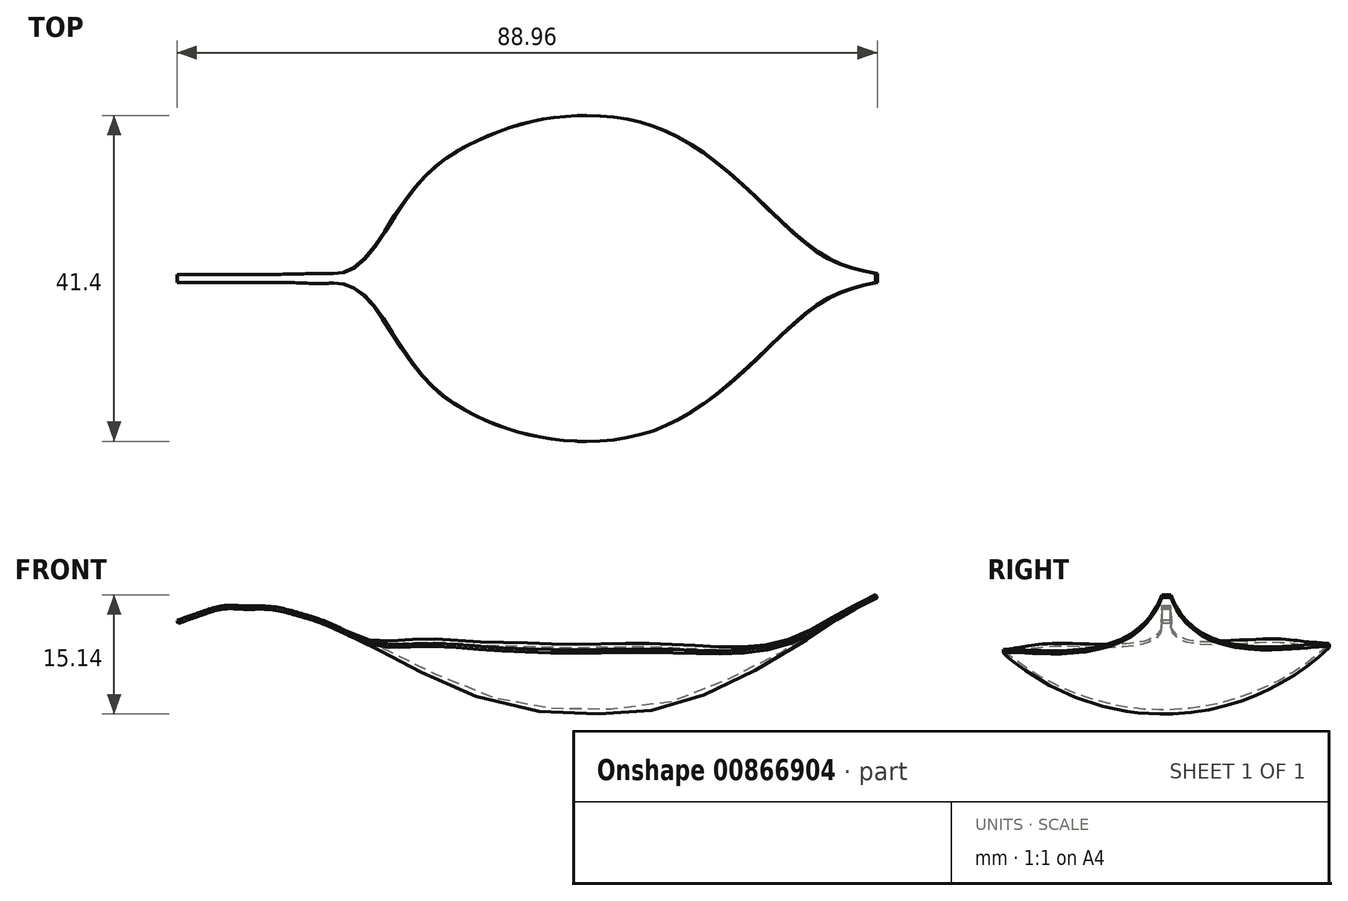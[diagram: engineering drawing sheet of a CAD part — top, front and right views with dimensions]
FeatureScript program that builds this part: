
annotation { "Feature Type Name" : "Feature", "Feature Type Description" : "" }
export const myFeature = defineFeature(function(context is Context, id is Id, definition is map)
    precondition{}
    {
        {
            var Q0;
            Q0=qCreatedBy(makeId("Front.planeOp"),FACE);
            var sketch = newSketch(context, id + "F0", { "sketchPlane" : qUnion([Q0])});
            skLineSegment(sketch, "E0", {"start": v(-44.39, 4.16) * mm, "end": v(-44.26, 3.85) * mm});
            skLineSegment(sketch, "E1", {"start": v(-44.39, 4.16) * mm, "end": v(-43.46, 4.53) * mm});
            skLineSegment(sketch, "E2", {"start": v(-41.78, 6.45) * mm, "end": v(-40.67, 3.2) * mm});
            skLineSegment(sketch, "E3", {"start": v(-38.43, 7.01) * mm, "end": v(-38.1, 3.57) * mm});
            skLineSegment(sketch, "E4", {"start": v(-35.95, 7.18) * mm, "end": v(-35.95, 3.55) * mm});
            skLineSegment(sketch, "E5", {"start": v(-32.27, 7.01) * mm, "end": v(-33.3, 3.24) * mm});
            skLineSegment(sketch, "E6", {"start": v(-28.95, 6.26) * mm, "end": v(-30.33, 2.84) * mm});
            skLineSegment(sketch, "E7", {"start": v(-25.44, 5.2) * mm, "end": v(-27.02, 1.8) * mm});
            skLineSegment(sketch, "E8", {"start": v(-22.43, 4.2) * mm, "end": v(-24.29, 0.87) * mm});
            skLineSegment(sketch, "E9", {"start": v(-19.09, 3.54) * mm, "end": v(-21.1, -0.4) * mm});
            skLineSegment(sketch, "E10", {"start": v(-15.92, 2.85) * mm, "end": v(-17.86, -1.91) * mm});
            skLineSegment(sketch, "E11", {"start": v(-11.9, 2.91) * mm, "end": v(-14.28, -3.81) * mm});
            skLineSegment(sketch, "E12", {"start": v(-6.26, 2.97) * mm, "end": v(-8.48, -6.69) * mm});
            skLineSegment(sketch, "E13", {"start": v(-0.4, 2.8) * mm, "end": v(-2.27, -8.54) * mm});
            skLineSegment(sketch, "E14", {"start": v(6.22, 2.3) * mm, "end": v(6.22, -9.83) * mm});
            skLineSegment(sketch, "E15", {"start": v(12.31, 2.74) * mm, "end": v(14.01, -9.61) * mm});
            skLineSegment(sketch, "E16", {"start": v(18.98, 3.06) * mm, "end": v(21.7, -7.59) * mm});
            skLineSegment(sketch, "E17", {"start": v(25.17, 3.1) * mm, "end": v(28.49, -5.53) * mm});
            skLineSegment(sketch, "E18", {"start": v(29.75, 3.12) * mm, "end": v(32.65, -3.36) * mm});
            skLineSegment(sketch, "E19", {"start": v(34.44, 4.54) * mm, "end": v(37.33, -0.72) * mm});
            skLineSegment(sketch, "E20", {"start": v(38.64, 6.73) * mm, "end": v(41.5, 2.56) * mm});
            skLineSegment(sketch, "E21", {"start": v(43, 9.56) * mm, "end": v(45.94, 5.03) * mm});
            skSolve(sketch);
        }
        {
            var Q0;
            Q0=makeQuery(id+"FtduOgnOkjfPjRU.importOp","IMPORT",FACE,{"importTag":1.0});
            cPoint(context, id + "F1", {"pointType" : PointType.MESH_POINT, "mesh" : qUnion([Q0]), "x" : -44.4 * mm, "y" : 0.48 * mm, "z" : 4.17 * mm});
        }
        {
            var Q0;
            Q0=makeQuery(id+"FtduOgnOkjfPjRU.importOp","IMPORT",EDGE,{"importTag":0.0});
            cPoint(context, id + "F2", {"pointType" : PointType.MESH_POINT, "mesh" : qUnion([Q0]), "x" : -44.4 * mm, "y" : -0.48 * mm, "z" : 4.15 * mm});
        }
        {
            var Q0;
            Q0=qCreatedBy(id+"F1",VERTEX);
            var Q1;
            Q1=qCreatedBy(id+"F2",VERTEX);
            var Q2;
            Q2=sQuery(id+"F0.wireOp",VERTEX,"E0.end");
            cPlane(context, id + "F3", {"entities" : qUnion([Q0, Q1, Q2]), "cplaneType" : CPlaneType.THREE_POINT, "offset" : 25.4 * mm, "width" : 152.4 * mm, "height" : 152.4 * mm});
        }
        {
            var Q0;
            Q0=qCreatedBy(id+"F3.planeOp",FACE);
            var sketch = newSketch(context, id + "F4", { "sketchPlane" : qUnion([Q0])});
            skLineSegment(sketch, "E22.bottom", {"start": v(-0.3, 20.4) * mm, "end": v(0.7, 20.4) * mm});
            skLineSegment(sketch, "E22.top", {"start": v(-0.3, 20) * mm, "end": v(0.7, 20) * mm});
            skLineSegment(sketch, "E22.left", {"start": v(-0.3, 20.4) * mm, "end": v(-0.3, 20) * mm});
            skLineSegment(sketch, "E22.right", {"start": v(0.7, 20.4) * mm, "end": v(0.7, 20) * mm});
            skLineSegment(sketch, "E23", {"start": v(0.2, 20.4) * mm, "end": v(0.2, 20) * mm, "construction": true});
            skSolve(sketch);
        }
        {
            var Q0;
            Q0=qCreatedBy(id+"F3.planeOp",FACE);
            var Q1;
            Q1=sQuery(id+"F0.wireOp",EDGE,"E2");
            cPlane(context, id + "F5", {"entities" : qUnion([Q0, Q1]), "cplaneType" : CPlaneType.LINE_ANGLE, "offset" : 25.4 * mm, "angle" : 0 * degree, "width" : 152.4 * mm, "height" : 152.4 * mm});
        }
        {
            var Q0;
            Q0=qCreatedBy(id+"F5.planeOp",FACE);
            var sketch = newSketch(context, id + "F6", { "sketchPlane" : qUnion([Q0])});
            skLineSegment(sketch, "E24.bottom", {"start": v(0.32, 18.53) * mm, "end": v(-0.7, 18.53) * mm});
            skLineSegment(sketch, "E24.top", {"start": v(0.32, 18.12) * mm, "end": v(-0.7, 18.12) * mm});
            skLineSegment(sketch, "E24.left", {"start": v(0.32, 18.53) * mm, "end": v(0.32, 18.12) * mm});
            skLineSegment(sketch, "E24.right", {"start": v(-0.7, 18.53) * mm, "end": v(-0.7, 18.12) * mm});
            skLineSegment(sketch, "E25", {"start": v(-0.19, 18.53) * mm, "end": v(-0.19, 18.12) * mm, "construction": true});
            skLineSegment(sketch, "E26", {"start": v(-0.7, 18.33) * mm, "end": v(-0.19, 18.33) * mm, "construction": true});
            skSolve(sketch);
        }
        {
            var Q0;
            Q0=qCreatedBy(id+"F5.planeOp",FACE);
            var Q1;
            Q1=sQuery(id+"F0.wireOp",EDGE,"E3");
            cPlane(context, id + "F7", {"entities" : qUnion([Q0, Q1]), "cplaneType" : CPlaneType.LINE_ANGLE, "offset" : 25.4 * mm, "angle" : 0 * degree, "width" : 152.4 * mm, "height" : 152.4 * mm});
        }
        {
            var Q0;
            Q0=qCreatedBy(id+"F7.planeOp",FACE);
            var sketch = newSketch(context, id + "F8", { "sketchPlane" : qUnion([Q0])});
            skLineSegment(sketch, "E27.bottom", {"start": v(-0.3, 9.7) * mm, "end": v(0.71, 9.7) * mm});
            skLineSegment(sketch, "E27.top", {"start": v(-0.3, 9.3) * mm, "end": v(0.71, 9.3) * mm});
            skLineSegment(sketch, "E27.left", {"start": v(-0.3, 9.7) * mm, "end": v(-0.3, 9.3) * mm});
            skLineSegment(sketch, "E27.right", {"start": v(0.71, 9.7) * mm, "end": v(0.71, 9.3) * mm});
            skSolve(sketch);
        }
        {
            var Q0;
            Q0=sQuery(id+"F0.wireOp",EDGE,"E4");
            var Q1;
            Q1=qCreatedBy(id+"F7.planeOp",FACE);
            cPlane(context, id + "F9", {"entities" : qUnion([Q0, Q1]), "cplaneType" : CPlaneType.LINE_ANGLE, "offset" : 25.4 * mm, "angle" : 0 * degree, "width" : 152.4 * mm, "height" : 152.4 * mm});
        }
        {
            var Q0;
            Q0=qCreatedBy(id+"F9.planeOp",FACE);
            var sketch = newSketch(context, id + "F10", { "sketchPlane" : qUnion([Q0])});
            skLineSegment(sketch, "E28.bottom", {"start": v(0.32, 6.18) * mm, "end": v(-0.7, 6.18) * mm});
            skLineSegment(sketch, "E28.top", {"start": v(0.32, 5.77) * mm, "end": v(-0.7, 5.77) * mm});
            skLineSegment(sketch, "E28.left", {"start": v(0.32, 6.18) * mm, "end": v(0.32, 5.77) * mm});
            skLineSegment(sketch, "E28.right", {"start": v(-0.7, 6.18) * mm, "end": v(-0.7, 5.77) * mm});
            skLineSegment(sketch, "E29", {"start": v(-0.19, 6.18) * mm, "end": v(-0.19, 5.77) * mm, "construction": true});
            skLineSegment(sketch, "E30", {"start": v(-0.7, 5.97) * mm, "end": v(-0.19, 5.97) * mm, "construction": true});
            skSolve(sketch);
        }
        {
            var Q0;
            Q0=qCreatedBy(id+"F9.planeOp",FACE);
            var Q1;
            Q1=sQuery(id+"F0.wireOp",EDGE,"E5");
            cPlane(context, id + "F11", {"entities" : qUnion([Q0, Q1]), "cplaneType" : CPlaneType.LINE_ANGLE, "offset" : 25.4 * mm, "angle" : 0 * degree, "width" : 152.4 * mm, "height" : 152.4 * mm});
        }
        {
            var Q0;
            Q0=qCreatedBy(id+"F11.planeOp",FACE);
            var sketch = newSketch(context, id + "F12", { "sketchPlane" : qUnion([Q0])});
            skLineSegment(sketch, "E31.bottom", {"start": v(-0.34, -2.64) * mm, "end": v(0.7, -2.64) * mm});
            skLineSegment(sketch, "E31.top", {"start": v(-0.34, -3.05) * mm, "end": v(0.7, -3.05) * mm});
            skLineSegment(sketch, "E31.left", {"start": v(-0.34, -2.64) * mm, "end": v(-0.34, -3.05) * mm});
            skLineSegment(sketch, "E31.right", {"start": v(0.7, -2.64) * mm, "end": v(0.7, -3.05) * mm});
            skSolve(sketch);
        }
        {
            var Q0;
            Q0=qCreatedBy(id+"F11.planeOp",FACE);
            var Q1;
            Q1=sQuery(id+"F0.wireOp",EDGE,"E6");
            cPlane(context, id + "F13", {"entities" : qUnion([Q0, Q1]), "cplaneType" : CPlaneType.LINE_ANGLE, "offset" : 25.4 * mm, "angle" : 0 * degree, "width" : 152.4 * mm, "height" : 152.4 * mm});
        }
        {
            var Q0;
            Q0=qCreatedBy(id+"F13.planeOp",FACE);
            var sketch = newSketch(context, id + "F14", { "sketchPlane" : qUnion([Q0])});
            skLineSegment(sketch, "E32.bottom", {"start": v(0.4, -5.99) * mm, "end": v(-0.72, -5.99) * mm});
            skLineSegment(sketch, "E32.top", {"start": v(0.4, -6.4) * mm, "end": v(-0.72, -6.4) * mm});
            skLineSegment(sketch, "E32.left", {"start": v(0.4, -5.99) * mm, "end": v(0.4, -6.4) * mm});
            skLineSegment(sketch, "E32.right", {"start": v(-0.72, -5.99) * mm, "end": v(-0.72, -6.4) * mm});
            skSolve(sketch);
        }
        {
            var Q0;
            Q0=qCreatedBy(id+"F13.planeOp",FACE);
            var Q1;
            Q1=sQuery(id+"F0.wireOp",EDGE,"E7");
            cPlane(context, id + "F15", {"entities" : qUnion([Q0, Q1]), "cplaneType" : CPlaneType.LINE_ANGLE, "offset" : 25.4 * mm, "angle" : 0 * degree, "width" : 152.4 * mm, "height" : 152.4 * mm});
        }
        {
            var Q0;
            Q0=qCreatedBy(id+"F15.planeOp",FACE);
            var sketch = newSketch(context, id + "F16", { "sketchPlane" : qUnion([Q0])});
            skLineSegment(sketch, "E33.bottom", {"start": v(-0.5, -6.99) * mm, "end": v(0.77, -6.99) * mm});
            skLineSegment(sketch, "E33.top", {"start": v(-0.5, -7.4) * mm, "end": v(0.77, -7.4) * mm});
            skLineSegment(sketch, "E33.left", {"start": v(-0.5, -6.99) * mm, "end": v(-0.5, -7.4) * mm});
            skLineSegment(sketch, "E33.right", {"start": v(0.77, -6.99) * mm, "end": v(0.77, -7.4) * mm});
            skSolve(sketch);
        }
        {
            var Q0;
            Q0=qCreatedBy(id+"F15.planeOp",FACE);
            var Q1;
            Q1=sQuery(id+"F0.wireOp",EDGE,"E8");
            cPlane(context, id + "F17", {"entities" : qUnion([Q0, Q1]), "cplaneType" : CPlaneType.LINE_ANGLE, "offset" : 25.4 * mm, "angle" : 0 * degree, "width" : 152.4 * mm, "height" : 152.4 * mm});
        }
        {
            var Q0;
            Q0=qCreatedBy(id+"F17.planeOp",FACE);
            var sketch = newSketch(context, id + "F18", { "sketchPlane" : qUnion([Q0])});
            skLineSegment(sketch, "E34.bottom", {"start": v(0.68, -8.57) * mm, "end": v(-0.89, -8.57) * mm});
            skLineSegment(sketch, "E34.top", {"start": v(0.68, -8.97) * mm, "end": v(-0.89, -8.97) * mm});
            skLineSegment(sketch, "E34.left", {"start": v(0.68, -8.57) * mm, "end": v(0.68, -8.97) * mm});
            skLineSegment(sketch, "E34.right", {"start": v(-0.89, -8.57) * mm, "end": v(-0.89, -8.97) * mm});
            skSolve(sketch);
        }
        {
            var Q0;
            Q0=qCreatedBy(id+"F17.planeOp",FACE);
            var Q1;
            Q1=sQuery(id+"F0.wireOp",EDGE,"E9");
            cPlane(context, id + "F19", {"entities" : qUnion([Q0, Q1]), "cplaneType" : CPlaneType.LINE_ANGLE, "offset" : 25.4 * mm, "angle" : 0 * degree, "width" : 152.4 * mm, "height" : 152.4 * mm});
        }
        {
            var Q0;
            Q0=qCreatedBy(id+"F19.planeOp",FACE);
            var sketch = newSketch(context, id + "F20", { "sketchPlane" : qUnion([Q0])});
            skLineSegment(sketch, "E35", {"start": v(2.82, -7.57) * mm, "end": v(2.82, -7.97) * mm});
            skLineSegment(sketch, "E36", {"start": v(-3.04, -7.45) * mm, "end": v(-3.04, -7.86) * mm});
            skArc(sketch, "E37", {"start": v(-3.04, -7.86) * mm, "mid": v(-0.11, -8.09) * mm, "end": v(2.82, -7.97) * mm});
            skArc(sketch, "E38", {"start": v(-3.04, -7.45) * mm, "mid": v(-0.11, -7.68) * mm, "end": v(2.82, -7.57) * mm});
            skSolve(sketch);
        }
        {
            var Q0;
            Q0=qCreatedBy(id+"F19.planeOp",FACE);
            var Q1;
            Q1=sQuery(id+"F0.wireOp",EDGE,"E10");
            cPlane(context, id + "F21", {"entities" : qUnion([Q0, Q1]), "cplaneType" : CPlaneType.LINE_ANGLE, "offset" : 25.4 * mm, "angle" : 0 * degree, "width" : 152.4 * mm, "height" : 152.4 * mm});
        }
        {
            var Q0;
            Q0=qCreatedBy(id+"F21.planeOp",FACE);
            var sketch = newSketch(context, id + "F22", { "sketchPlane" : qUnion([Q0])});
            skLineSegment(sketch, "E39", {"start": v(8.5, -4.5) * mm, "end": v(8.5, -4.9) * mm});
            skLineSegment(sketch, "E40", {"start": v(-7.76, -5.08) * mm, "end": v(-7.76, -5.49) * mm});
            skArc(sketch, "E41", {"start": v(-7.76, -5.49) * mm, "mid": v(0.42, -6.68) * mm, "end": v(8.5, -4.9) * mm});
            skArc(sketch, "E42", {"start": v(-7.76, -5.08) * mm, "mid": v(0.42, -6.24) * mm, "end": v(8.5, -4.5) * mm});
            skSolve(sketch);
        }
        {
            var Q0;
            Q0=qCreatedBy(id+"F21.planeOp",FACE);
            var Q1;
            Q1=sQuery(id+"F0.wireOp",EDGE,"E11");
            cPlane(context, id + "F23", {"entities" : qUnion([Q0, Q1]), "cplaneType" : CPlaneType.LINE_ANGLE, "offset" : 25.4 * mm, "angle" : 0 * degree, "width" : 152.4 * mm, "height" : 152.4 * mm});
        }
        {
            var Q0;
            Q0=qCreatedBy(id+"F23.planeOp",FACE);
            var sketch = newSketch(context, id + "F24", { "sketchPlane" : qUnion([Q0])});
            skLineSegment(sketch, "E43", {"start": v(-13.64, -2.2) * mm, "end": v(-13.64, -2.6) * mm});
            skLineSegment(sketch, "E44", {"start": v(13.22, -2.84) * mm, "end": v(13.22, -3.24) * mm});
            skArc(sketch, "E45", {"start": v(-13.64, -2.6) * mm, "mid": v(-0.3, -6.56) * mm, "end": v(13.22, -3.24) * mm});
            skArc(sketch, "E46", {"start": v(-13.64, -2.2) * mm, "mid": v(-0.3, -6.03) * mm, "end": v(13.22, -2.84) * mm});
            skSolve(sketch);
        }
        {
            var Q0;
            Q0=qCreatedBy(id+"F23.planeOp",FACE);
            var Q1;
            Q1=sQuery(id+"F0.wireOp",EDGE,"E12");
            cPlane(context, id + "F25", {"entities" : qUnion([Q0, Q1]), "cplaneType" : CPlaneType.LINE_ANGLE, "offset" : 25.4 * mm, "angle" : 0 * degree, "width" : 152.4 * mm, "height" : 152.4 * mm});
        }
        {
            var Q0;
            Q0=qCreatedBy(id+"F25.planeOp",FACE);
            var sketch = newSketch(context, id + "F26", { "sketchPlane" : qUnion([Q0])});
            skLineSegment(sketch, "E47", {"start": v(17.36, 0.18) * mm, "end": v(17.36, -0.23) * mm});
            skLineSegment(sketch, "E48", {"start": v(-17.33, -0.44) * mm, "end": v(-17.33, -0.84) * mm});
            skArc(sketch, "E49", {"start": v(-17.33, -0.84) * mm, "mid": v(0.12, -6.34) * mm, "end": v(17.36, -0.23) * mm});
            skArc(sketch, "E50", {"start": v(-17.33, -0.44) * mm, "mid": v(0.12, -5.69) * mm, "end": v(17.36, 0.18) * mm});
            skSolve(sketch);
        }
        {
            var Q0;
            Q0=qCreatedBy(id+"F25.planeOp",FACE);
            var Q1;
            Q1=sQuery(id+"F0.wireOp",EDGE,"E13");
            cPlane(context, id + "F27", {"entities" : qUnion([Q0, Q1]), "cplaneType" : CPlaneType.LINE_ANGLE, "offset" : 25.4 * mm, "angle" : 0 * degree, "width" : 152.4 * mm, "height" : 152.4 * mm});
        }
        {
            var Q0;
            Q0=qCreatedBy(id+"F27.planeOp",FACE);
            var sketch = newSketch(context, id + "F28", { "sketchPlane" : qUnion([Q0])});
            skLineSegment(sketch, "E51", {"start": v(-19.65, 1.37) * mm, "end": v(-19.65, 0.96) * mm});
            skLineSegment(sketch, "E52", {"start": v(19.58, 0.61) * mm, "end": v(19.58, 0.2) * mm});
            skArc(sketch, "E53", {"start": v(-19.65, 0.96) * mm, "mid": v(-0.18, -6.9) * mm, "end": v(19.58, 0.2) * mm});
            skArc(sketch, "E54", {"start": v(-19.65, 1.37) * mm, "mid": v(-0.18, -6.32) * mm, "end": v(19.58, 0.61) * mm});
            skSolve(sketch);
        }
        {
            var Q0;
            Q0=sQuery(id+"F0.wireOp",EDGE,"E14");
            var Q1;
            Q1=qCreatedBy(id+"F27.planeOp",FACE);
            cPlane(context, id + "F29", {"entities" : qUnion([Q0, Q1]), "cplaneType" : CPlaneType.LINE_ANGLE, "offset" : 25.4 * mm, "angle" : 0 * degree, "width" : 152.4 * mm, "height" : 152.4 * mm});
        }
        {
            var Q0;
            Q0=qCreatedBy(id+"F29.planeOp",FACE);
            var sketch = newSketch(context, id + "F30", { "sketchPlane" : qUnion([Q0])});
            skLineSegment(sketch, "E55", {"start": v(20.7, 1.32) * mm, "end": v(20.7, 0.91) * mm});
            skLineSegment(sketch, "E56", {"start": v(-20.64, 0.61) * mm, "end": v(-20.64, 0.2) * mm});
            skArc(sketch, "E57", {"start": v(-20.64, 0.2) * mm, "mid": v(0.17, -7.5) * mm, "end": v(20.7, 0.91) * mm});
            skArc(sketch, "E58", {"start": v(-20.64, 0.61) * mm, "mid": v(0.17, -6.93) * mm, "end": v(20.7, 1.32) * mm});
            skSolve(sketch);
        }
        {
            var Q0;
            Q0=qCreatedBy(id+"F29.planeOp",FACE);
            var Q1;
            Q1=sQuery(id+"F0.wireOp",EDGE,"E15");
            cPlane(context, id + "F31", {"entities" : qUnion([Q0, Q1]), "cplaneType" : CPlaneType.LINE_ANGLE, "offset" : 25.4 * mm, "angle" : 0 * degree, "width" : 152.4 * mm, "height" : 152.4 * mm});
        }
        {
            var Q0;
            Q0=qCreatedBy(id+"F31.planeOp",FACE);
            var sketch = newSketch(context, id + "F32", { "sketchPlane" : qUnion([Q0])});
            skLineSegment(sketch, "E59", {"start": v(20.2, -1.05) * mm, "end": v(20.2, -1.45) * mm});
            skLineSegment(sketch, "E60", {"start": v(-20.33, -0.3) * mm, "end": v(-20.33, -0.72) * mm});
            skArc(sketch, "E61", {"start": v(-20.33, -0.72) * mm, "mid": v(-0.21, -9.15) * mm, "end": v(20.2, -1.45) * mm});
            skArc(sketch, "E62", {"start": v(-20.33, -0.3) * mm, "mid": v(-0.2, -8.5) * mm, "end": v(20.2, -1.05) * mm});
            skSolve(sketch);
        }
        {
            var Q0;
            Q0=qCreatedBy(id+"F31.planeOp",FACE);
            var Q1;
            Q1=sQuery(id+"F0.wireOp",EDGE,"E16");
            cPlane(context, id + "F33", {"entities" : qUnion([Q0, Q1]), "cplaneType" : CPlaneType.LINE_ANGLE, "offset" : 25.4 * mm, "angle" : 0 * degree, "width" : 152.4 * mm, "height" : 152.4 * mm});
        }
        {
            var Q0;
            Q0=qCreatedBy(id+"F33.planeOp",FACE);
            var sketch = newSketch(context, id + "F34", { "sketchPlane" : qUnion([Q0])});
            skLineSegment(sketch, "E63", {"start": v(-17.66, -4.26) * mm, "end": v(-17.66, -4.66) * mm});
            skLineSegment(sketch, "E64", {"start": v(17.85, -3.64) * mm, "end": v(17.85, -4.05) * mm});
            skArc(sketch, "E65", {"start": v(-17.66, -4.66) * mm, "mid": v(0.2, -10.69) * mm, "end": v(17.85, -4.05) * mm});
            skArc(sketch, "E66", {"start": v(-17.66, -4.26) * mm, "mid": v(0.2, -10.2) * mm, "end": v(17.85, -3.64) * mm});
            skSolve(sketch);
        }
        {
            var Q0;
            Q0=sQuery(id+"F0.wireOp",EDGE,"E17");
            var Q1;
            Q1=qCreatedBy(id+"F33.planeOp",FACE);
            cPlane(context, id + "F35", {"entities" : qUnion([Q0, Q1]), "cplaneType" : CPlaneType.LINE_ANGLE, "offset" : 25.4 * mm, "angle" : 0 * degree, "width" : 152.4 * mm, "height" : 152.4 * mm});
        }
        {
            var Q0;
            Q0=qCreatedBy(id+"F35.planeOp",FACE);
            var sketch = newSketch(context, id + "F36", { "sketchPlane" : qUnion([Q0])});
            skLineSegment(sketch, "E67", {"start": v(12.88, -8.88) * mm, "end": v(12.88, -9.3) * mm});
            skLineSegment(sketch, "E68", {"start": v(-13.17, -8.45) * mm, "end": v(-13.17, -8.85) * mm});
            skArc(sketch, "E69", {"start": v(-13.17, -8.85) * mm, "mid": v(-0.2, -12.42) * mm, "end": v(12.88, -9.3) * mm});
            skArc(sketch, "E70", {"start": v(-13.17, -8.45) * mm, "mid": v(-0.2, -11.9) * mm, "end": v(12.88, -8.88) * mm});
            skSolve(sketch);
        }
        {
            var Q0;
            Q0=qCreatedBy(id+"F35.planeOp",FACE);
            var Q1;
            Q1=sQuery(id+"F0.wireOp",EDGE,"E18");
            cPlane(context, id + "F37", {"entities" : qUnion([Q0, Q1]), "cplaneType" : CPlaneType.LINE_ANGLE, "offset" : 25.4 * mm, "angle" : 0 * degree, "width" : 152.4 * mm, "height" : 152.4 * mm});
        }
        {
            var Q0;
            Q0=qCreatedBy(id+"F37.planeOp",FACE);
            var sketch = newSketch(context, id + "F38", { "sketchPlane" : qUnion([Q0])});
            skLineSegment(sketch, "E71", {"start": v(-8.58, -11.61) * mm, "end": v(-8.58, -12.02) * mm});
            skLineSegment(sketch, "E72", {"start": v(8.93, -11.33) * mm, "end": v(8.93, -11.74) * mm});
            skArc(sketch, "E73", {"start": v(-8.58, -12.02) * mm, "mid": v(0.2, -13.45) * mm, "end": v(8.93, -11.74) * mm});
            skArc(sketch, "E74", {"start": v(-8.58, -11.61) * mm, "mid": v(0.2, -13.03) * mm, "end": v(8.93, -11.33) * mm});
            skSolve(sketch);
        }
        {
            var Q0;
            Q0=sQuery(id+"F0.wireOp",EDGE,"E19");
            var Q1;
            Q1=qCreatedBy(id+"F37.planeOp",FACE);
            cPlane(context, id + "F39", {"entities" : qUnion([Q0, Q1]), "cplaneType" : CPlaneType.LINE_ANGLE, "offset" : 25.4 * mm, "angle" : 0 * degree, "width" : 152.4 * mm, "height" : 152.4 * mm});
        }
        {
            var Q0;
            Q0=qCreatedBy(id+"F39.planeOp",FACE);
            var sketch = newSketch(context, id + "F40", { "sketchPlane" : qUnion([Q0])});
            skLineSegment(sketch, "E75", {"start": v(-4.58, -14.56) * mm, "end": v(-4.58, -14.97) * mm});
            skLineSegment(sketch, "E76", {"start": v(4.2, -14.7) * mm, "end": v(4.2, -15.1) * mm});
            skArc(sketch, "E77", {"start": v(-4.58, -14.97) * mm, "mid": v(-0.2, -15.44) * mm, "end": v(4.2, -15.1) * mm});
            skArc(sketch, "E78", {"start": v(-4.58, -14.56) * mm, "mid": v(-0.2, -15) * mm, "end": v(4.2, -14.7) * mm});
            skSolve(sketch);
        }
        {
            var Q0;
            Q0=sQuery(id+"F0.wireOp",EDGE,"E20");
            var Q1;
            Q1=qCreatedBy(id+"F39.planeOp",FACE);
            cPlane(context, id + "F41", {"entities" : qUnion([Q0, Q1]), "cplaneType" : CPlaneType.LINE_ANGLE, "offset" : 25.4 * mm, "angle" : 0 * degree, "width" : 152.4 * mm, "height" : 152.4 * mm});
        }
        {
            var Q0;
            Q0=qCreatedBy(id+"F41.planeOp",FACE);
            var sketch = newSketch(context, id + "F42", { "sketchPlane" : qUnion([Q0])});
            skLineSegment(sketch, "E79", {"start": v(-1.6, -18.18) * mm, "end": v(-1.6, -18.59) * mm});
            skLineSegment(sketch, "E80", {"start": v(2.03, -18.12) * mm, "end": v(2.03, -18.53) * mm});
            skArc(sketch, "E81", {"start": v(-1.6, -18.59) * mm, "mid": v(0.21, -18.63) * mm, "end": v(2.03, -18.53) * mm});
            skArc(sketch, "E82", {"start": v(-1.6, -18.18) * mm, "mid": v(0.21, -18.21) * mm, "end": v(2.03, -18.12) * mm});
            skSolve(sketch);
        }
        {
            var Q0;
            Q0=qCreatedBy(id+"F41.planeOp",FACE);
            var Q1;
            Q1=sQuery(id+"F0.wireOp",EDGE,"E21");
            cPlane(context, id + "F43", {"entities" : qUnion([Q0, Q1]), "cplaneType" : CPlaneType.LINE_ANGLE, "offset" : 25.4 * mm, "angle" : 0 * degree, "width" : 152.4 * mm, "height" : 152.4 * mm});
        }
        {
            var Q0;
            Q0=qCreatedBy(id+"F43.planeOp",FACE);
            var sketch = newSketch(context, id + "F44", { "sketchPlane" : qUnion([Q0])});
            skLineSegment(sketch, "E83.bottom", {"start": v(0.28, -17.8) * mm, "end": v(-0.85, -17.8) * mm});
            skLineSegment(sketch, "E83.top", {"start": v(0.28, -18.2) * mm, "end": v(-0.85, -18.2) * mm});
            skLineSegment(sketch, "E83.left", {"start": v(0.28, -17.8) * mm, "end": v(0.28, -18.2) * mm});
            skLineSegment(sketch, "E83.right", {"start": v(-0.85, -17.8) * mm, "end": v(-0.85, -18.2) * mm});
            skSolve(sketch);
        }
        {
            var Q0;
            Q0=qSketchRegion(id+"F4",true);
            var Q1;
            Q1=qSketchRegion(id+"F6",true);
            var Q2;
            Q2=qSketchRegion(id+"F8",true);
            var Q3;
            Q3=qSketchRegion(id+"F10",true);
            var Q4;
            Q4=qSketchRegion(id+"F12",true);
            var Q5;
            Q5=qSketchRegion(id+"F14",true);
            var Q6;
            Q6=qSketchRegion(id+"F16",true);
            var Q7;
            Q7=qSketchRegion(id+"F18",true);
            var Q8;
            Q8=qSketchRegion(id+"F20",true);
            var Q9;
            Q9=qSketchRegion(id+"F22",true);
            var Q10;
            Q10=qSketchRegion(id+"F24",true);
            var Q11;
            Q11=qSketchRegion(id+"F26",true);
            var Q12;
            Q12=qSketchRegion(id+"F28",true);
            var Q13;
            Q13=qSketchRegion(id+"F30",true);
            var Q14;
            Q14=qSketchRegion(id+"F32",true);
            var Q15;
            Q15=qSketchRegion(id+"F34",true);
            var Q16;
            Q16=qSketchRegion(id+"F36",true);
            var Q17;
            Q17=qSketchRegion(id+"F38",true);
            var Q18;
            Q18=qSketchRegion(id+"F40",true);
            var Q19;
            Q19=qSketchRegion(id+"F42",true);
            var Q20;
            Q20=qSketchRegion(id+"F44",true);
            loft(context, id + "F45", {"sheetProfilesArray" : [{ "sheetProfileEntities" : qUnion([Q0]) }, { "sheetProfileEntities" : qUnion([Q1]) }, { "sheetProfileEntities" : qUnion([Q2]) }, { "sheetProfileEntities" : qUnion([Q3]) }, { "sheetProfileEntities" : qUnion([Q4]) }, { "sheetProfileEntities" : qUnion([Q5]) }, { "sheetProfileEntities" : qUnion([Q6]) }, { "sheetProfileEntities" : qUnion([Q7]) }, { "sheetProfileEntities" : qUnion([Q8]) }, { "sheetProfileEntities" : qUnion([Q9]) }, { "sheetProfileEntities" : qUnion([Q10]) }, { "sheetProfileEntities" : qUnion([Q11]) }, { "sheetProfileEntities" : qUnion([Q12]) }, { "sheetProfileEntities" : qUnion([Q13]) }, { "sheetProfileEntities" : qUnion([Q14]) }, { "sheetProfileEntities" : qUnion([Q15]) }, { "sheetProfileEntities" : qUnion([Q16]) }, { "sheetProfileEntities" : qUnion([Q17]) }, { "sheetProfileEntities" : qUnion([Q18]) }, { "sheetProfileEntities" : qUnion([Q19]) }, { "sheetProfileEntities" : qUnion([Q20]) }]});
        }
    });
